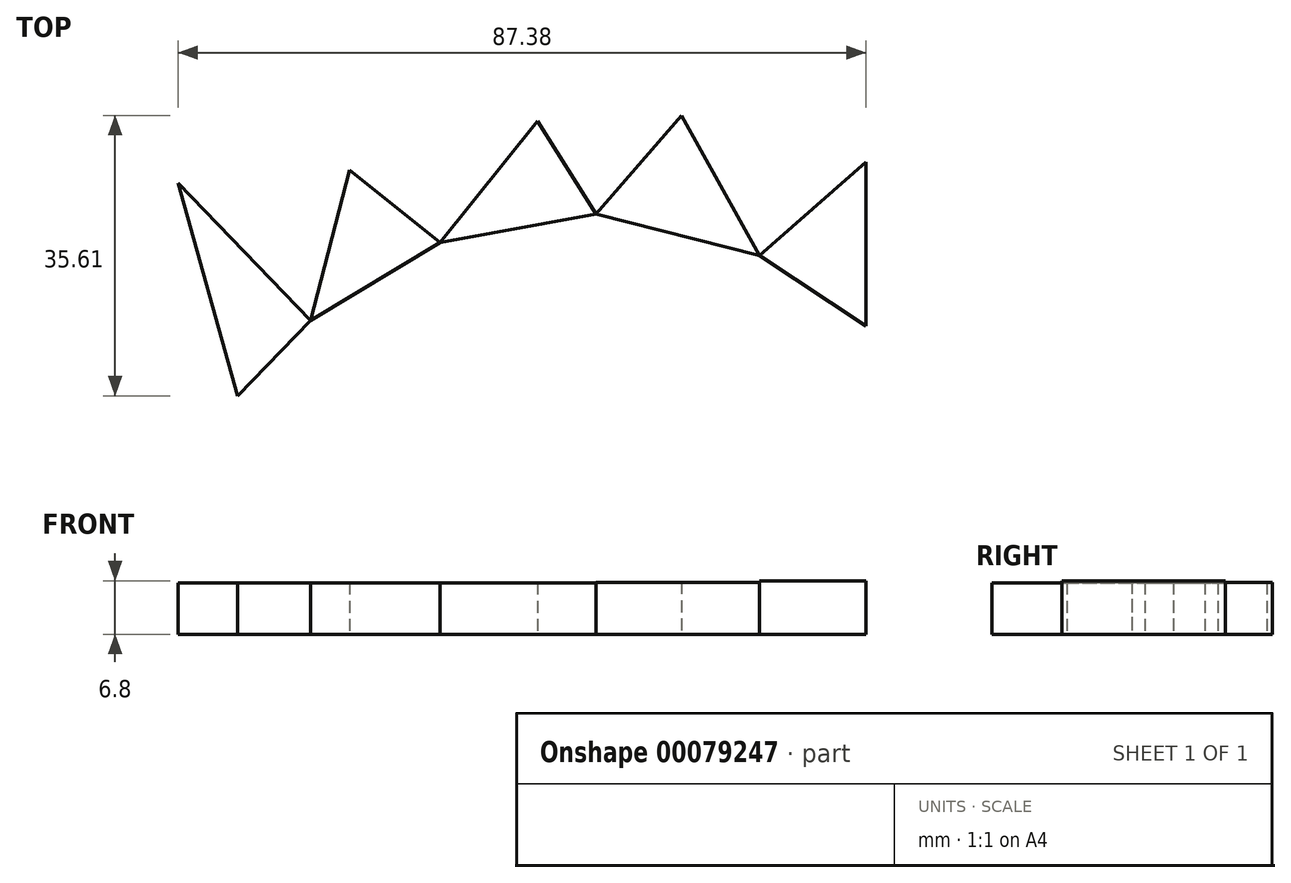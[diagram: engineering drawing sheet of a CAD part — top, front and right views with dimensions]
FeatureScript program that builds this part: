
annotation { "Feature Type Name" : "Feature", "Feature Type Description" : "" }
export const myFeature = defineFeature(function(context is Context, id is Id, definition is map)
    precondition{}
    {
        {
            var Q0;
            Q0=qCreatedBy(makeId("Top.planeOp"),FACE);
            var sketch = newSketch(context, id + "F0", { "sketchPlane" : qUnion([Q0])});
            skLineSegment(sketch, "E0", {"start": v(-41.34, 28.47) * mm, "end": v(-48.93, 55.5) * mm});
            skLineSegment(sketch, "E1", {"start": v(-48.93, 55.5) * mm, "end": v(-32.11, 38.03) * mm});
            skLineSegment(sketch, "E2", {"start": v(-32.11, 38.03) * mm, "end": v(-27.17, 57.15) * mm});
            skLineSegment(sketch, "E3", {"start": v(-27.17, 57.15) * mm, "end": v(-15.63, 47.92) * mm});
            skLineSegment(sketch, "E4", {"start": v(-15.63, 47.92) * mm, "end": v(-3.24, 63.4) * mm});
            skLineSegment(sketch, "E5", {"start": v(-3.24, 63.4) * mm, "end": v(4.16, 51.55) * mm});
            skLineSegment(sketch, "E6", {"start": v(4.16, 51.55) * mm, "end": v(15.04, 64.08) * mm});
            skLineSegment(sketch, "E7", {"start": v(15.04, 64.08) * mm, "end": v(24.93, 46.27) * mm});
            skLineSegment(sketch, "E8", {"start": v(24.93, 46.27) * mm, "end": v(38.45, 58.14) * mm});
            skLineSegment(sketch, "E9", {"start": v(38.45, 58.14) * mm, "end": v(38.45, 37.37) * mm});
            skLineSegment(sketch, "E10", {"start": v(-41.34, 28.47) * mm, "end": v(-32.11, 38.03) * mm});
            skLineSegment(sketch, "E11", {"start": v(-15.63, 47.92) * mm, "end": v(-32.11, 38.03) * mm});
            skLineSegment(sketch, "E12", {"start": v(-15.63, 47.92) * mm, "end": v(4.16, 51.55) * mm});
            skLineSegment(sketch, "E13", {"start": v(4.16, 51.55) * mm, "end": v(24.93, 46.27) * mm});
            skLineSegment(sketch, "E14", {"start": v(24.93, 46.27) * mm, "end": v(38.45, 37.37) * mm});
            skSolve(sketch);
        }
        {
            var Q0;
            Q0=makeQuery(id+"F0.imprint","IMPRINT",FACE,{"disambiguationData":[TD([[makeQuery(id+"F0.imprint","IMPRINT",EDGE,{"derivedFrom":sQuery(id+"F0.wireOp",EDGE,"E0")}),-1.0]])]});
            extrude(context, id + "F1", {"entities" : qUnion([Q0]), "depth" : 6.55 * mm});
        }
        {
            var Q0;
            Q0=makeQuery(id+"F0.imprint","IMPRINT",FACE,{"disambiguationData":[TD([[makeQuery(id+"F0.imprint","IMPRINT",EDGE,{"derivedFrom":sQuery(id+"F0.wireOp",EDGE,"E2")}),-1.0]])]});
            extrude(context, id + "F2", {"entities" : qUnion([Q0]), "depth" : 6.55 * mm});
        }
        {
            var Q0;
            Q0=makeQuery(id+"F0.imprint","IMPRINT",FACE,{"disambiguationData":[TD([[makeQuery(id+"F0.imprint","IMPRINT",EDGE,{"derivedFrom":sQuery(id+"F0.wireOp",EDGE,"E4")}),-1.0]])]});
            extrude(context, id + "F3", {"entities" : qUnion([Q0]), "depth" : 6.55 * mm});
        }
        {
            var Q0;
            Q0=makeQuery(id+"F0.imprint","IMPRINT",FACE,{"disambiguationData":[TD([[makeQuery(id+"F0.imprint","IMPRINT",EDGE,{"derivedFrom":sQuery(id+"F0.wireOp",EDGE,"E6")}),-1.0]])]});
            extrude(context, id + "F4", {"entities" : qUnion([Q0]), "depth" : 6.61 * mm});
        }
        {
            var Q0;
            Q0=makeQuery(id+"F0.imprint","IMPRINT",FACE,{"disambiguationData":[TD([[makeQuery(id+"F0.imprint","IMPRINT",EDGE,{"derivedFrom":sQuery(id+"F0.wireOp",EDGE,"E8")}),-1.0]])]});
            extrude(context, id + "F5", {"entities" : qUnion([Q0]), "depth" : 6.8 * mm});
        }
    });
